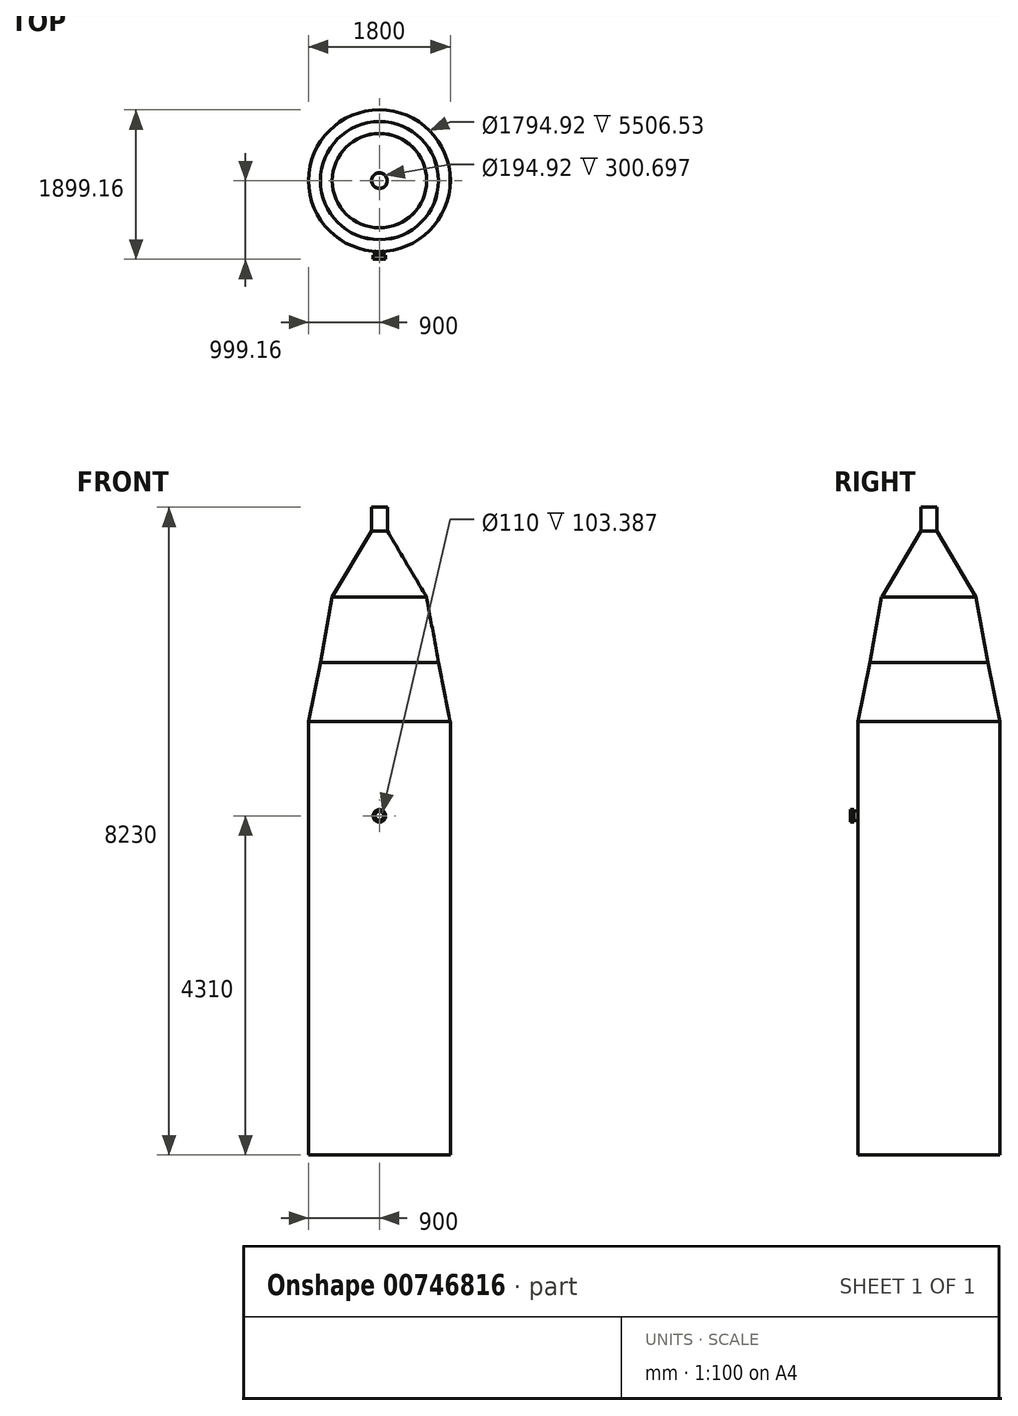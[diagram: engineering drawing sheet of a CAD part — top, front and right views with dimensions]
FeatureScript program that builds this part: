
annotation { "Feature Type Name" : "Feature", "Feature Type Description" : "" }
export const myFeature = defineFeature(function(context is Context, id is Id, definition is map)
    precondition{}
    {
        {
            var Q0;
            Q0=qCreatedBy(makeId("Top.planeOp"),FACE);
            var sketch = newSketch(context, id + "F0", { "sketchPlane" : qUnion([Q0])});
            skCircle(sketch, "E0", {"center": v(0, 0) * mm, "radius": 900 * mm});
            skSolve(sketch);
        }
        {
            var Q0;
            Q0=qSketchRegion(id+"F0",true);
            extrude(context, id + "F1", {"entities" : qUnion([Q0]), "depth" : 5510 * mm, "offsetDistance" : 25.4 * mm});
        }
        {
            var Q0;
            Q0=makeQuery(id+"F1.opExtrude","CAP_FACE",FACE,{"disambiguationData":[OSD([sQuery(id+"F0.wireOp",EDGE,"E0")])],"isStart":false});
            cPlane(context, id + "F2", {"entities" : qUnion([Q0]), "cplaneType" : CPlaneType.OFFSET, "offset" : 750 * mm, "width" : 152.4 * mm, "height" : 152.4 * mm});
        }
        {
            var Q0;
            Q0=qCreatedBy(id+"F2.planeOp",FACE);
            var sketch = newSketch(context, id + "F3", { "sketchPlane" : qUnion([Q0])});
            skCircle(sketch, "E1", {"center": v(0, 0) * mm, "radius": 750 * mm});
            skSolve(sketch);
        }
        {
            var Q0;
            Q0=makeQuery(id+"F3.imprint","IMPRINT",FACE,{"disambiguationData":[TD([[makeQuery(id+"F3.imprint","IMPRINT",EDGE,{"derivedFrom":sQuery(id+"F3.wireOp",EDGE,"E1")}),1.0]])]});
            var Q1;
            Q1=makeQuery(id+"F1.opExtrude","CAP_FACE",FACE,{"disambiguationData":[OSD([sQuery(id+"F0.wireOp",EDGE,"E0")])],"isStart":false});
            extrude(context, id + "F4", {"entities" : qUnion([Q0]), "operationType" : NewBodyOperationType.ADD, "endBound" : BoundingType.UP_TO_SURFACE, "oppositeDirection" : true, "depth" : 25.4 * mm, "endBoundEntityFace" : qUnion([Q1]), "offsetDistance" : 25.4 * mm, "hasDraft" : true, "draftAngle" : 11.3 * degree});
        }
        {
            var Q0;
            Q0=makeQuery(id+"F4.opExtrude","CAP_FACE",FACE,{"disambiguationData":[OSD([sQuery(id+"F3.wireOp",EDGE,"E1")])],"isStart":true});
            cPlane(context, id + "F5", {"entities" : qUnion([Q0]), "cplaneType" : CPlaneType.OFFSET, "offset" : 830 * mm, "width" : 152.4 * mm, "height" : 152.4 * mm});
        }
        {
            var Q0;
            Q0=qCreatedBy(id+"F5.planeOp",FACE);
            var sketch = newSketch(context, id + "F6", { "sketchPlane" : qUnion([Q0])});
            skCircle(sketch, "E2", {"center": v(0, 0) * mm, "radius": 600 * mm});
            skSolve(sketch);
        }
        {
            var Q0;
            Q0=qSketchRegion(id+"F6",true);
            var Q1;
            Q1=makeQuery(id+"F4.opExtrude","CAP_FACE",FACE,{"disambiguationData":[OSD([sQuery(id+"F3.wireOp",EDGE,"E1")])],"isStart":true});
            extrude(context, id + "F7", {"entities" : qUnion([Q0]), "operationType" : NewBodyOperationType.ADD, "endBound" : BoundingType.UP_TO_SURFACE, "oppositeDirection" : true, "depth" : 25.4 * mm, "endBoundEntityFace" : qUnion([Q1]), "offsetDistance" : 25.4 * mm, "hasDraft" : true, "draftAngle" : 10.2 * degree});
        }
        {
            var Q0;
            Q0=makeQuery(id+"F7.opExtrude","CAP_FACE",FACE,{"disambiguationData":[OSD([sQuery(id+"F6.wireOp",EDGE,"E2")])],"isStart":true});
            cPlane(context, id + "F8", {"entities" : qUnion([Q0]), "cplaneType" : CPlaneType.OFFSET, "offset" : 840 * mm, "width" : 152.4 * mm, "height" : 152.4 * mm});
        }
        {
            var Q0;
            Q0=qCreatedBy(id+"F8.planeOp",FACE);
            var sketch = newSketch(context, id + "F9", { "sketchPlane" : qUnion([Q0])});
            skCircle(sketch, "E3", {"center": v(0, 0) * mm, "radius": 100 * mm});
            skSolve(sketch);
        }
        {
            var Q0;
            Q0=qSketchRegion(id+"F9",true);
            var Q1;
            Q1=makeQuery(id+"F7.opExtrude","CAP_FACE",FACE,{"disambiguationData":[OSD([sQuery(id+"F6.wireOp",EDGE,"E2")])],"isStart":true});
            extrude(context, id + "F10", {"entities" : qUnion([Q0]), "operationType" : NewBodyOperationType.ADD, "endBound" : BoundingType.UP_TO_SURFACE, "oppositeDirection" : true, "depth" : 25.4 * mm, "endBoundEntityFace" : qUnion([Q1]), "offsetDistance" : 25.4 * mm, "hasDraft" : true, "draftAngle" : 30.7 * degree});
        }
        {
            var Q0;
            Q0=makeQuery(id+"F10.opExtrude","CAP_FACE",FACE,{"disambiguationData":[OSD([sQuery(id+"F9.wireOp",EDGE,"E3")])],"isStart":true});
            var sketch = newSketch(context, id + "F11", { "sketchPlane" : qUnion([Q0])});
            skCircle(sketch, "E4", {"center": v(0, 0) * mm, "radius": 100 * mm});
            skSolve(sketch);
        }
        {
            var Q0;
            Q0=qSketchRegion(id+"F11",true);
            extrude(context, id + "F12", {"entities" : qUnion([Q0]), "operationType" : NewBodyOperationType.ADD, "depth" : 300 * mm, "offsetDistance" : 25.4 * mm});
        }
        {
            var Q0;
            Q0=makeQuery(id+"F12.opExtrude","CAP_FACE",FACE,{"disambiguationData":[OSD([sQuery(id+"F11.wireOp",EDGE,"E4")])],"isStart":false});
            shell(context, id + "F13", {"entities" : qUnion([Q0]), "thickness" : 2.54 * mm});
        }
        {
            var Q0;
            Q0=qCreatedBy(makeId("Front.planeOp"),FACE);
            cPlane(context, id + "F14", {"entities" : qUnion([Q0]), "cplaneType" : CPlaneType.OFFSET, "offset" : 899.16 * mm, "width" : 152.4 * mm, "height" : 152.4 * mm});
        }
        {
            var Q0;
            Q0=qCreatedBy(id+"F14.planeOp",FACE);
            var sketch = newSketch(context, id + "F15", { "sketchPlane" : qUnion([Q0])});
            skCircle(sketch, "E5", {"center": v(0, 4310) * mm, "radius": 60 * mm});
            skSolve(sketch);
        }
        {
            var Q0;
            Q0 = qSketchRegion(id + "F15", true);
            extrude(context, id + "F16", {"entities" : qUnion([Q0]), "operationType" : NewBodyOperationType.ADD, "depth" : 50 * mm, "offsetDistance" : 25.4 * mm});
        }
        {
            var Q0;
            Q0=makeQuery(id+"F16.opExtrude","CAP_FACE",FACE,{"disambiguationData":[OSD([sQuery(id+"F15.wireOp",EDGE,"E5")])],"isStart":false});
            var sketch = newSketch(context, id + "F17", { "sketchPlane" : qUnion([Q0])});
            skCircle(sketch, "E6", {"center": v(0, 4310) * mm, "radius": 80 * mm});
            skSolve(sketch);
        }
        {
            var Q0;
            Q0 = qSketchRegion(id + "F17", true);
            extrude(context, id + "F18", {"entities" : qUnion([Q0]), "operationType" : NewBodyOperationType.ADD, "depth" : 50 * mm, "offsetDistance" : 25.4 * mm});
        }
        {
            var Q0;
            Q0=makeQuery(id+"F18.opExtrude","CAP_FACE",FACE,{"disambiguationData":[OSD([sQuery(id+"F17.wireOp",EDGE,"E6")])],"isStart":false});
            var sketch = newSketch(context, id + "F19", { "sketchPlane" : qUnion([Q0])});
            skCircle(sketch, "E7", {"center": v(0, 4310) * mm, "radius": 55 * mm});
            skSolve(sketch);
        }
        {
            var Q0;
            Q0 = qSketchRegion(id + "F19", true);
            extrude(context, id + "F20", {"entities" : qUnion([Q0]), "operationType" : NewBodyOperationType.REMOVE, "oppositeDirection" : true, "depth" : 208.28 * mm, "offsetDistance" : 25.4 * mm});
        }
    });
